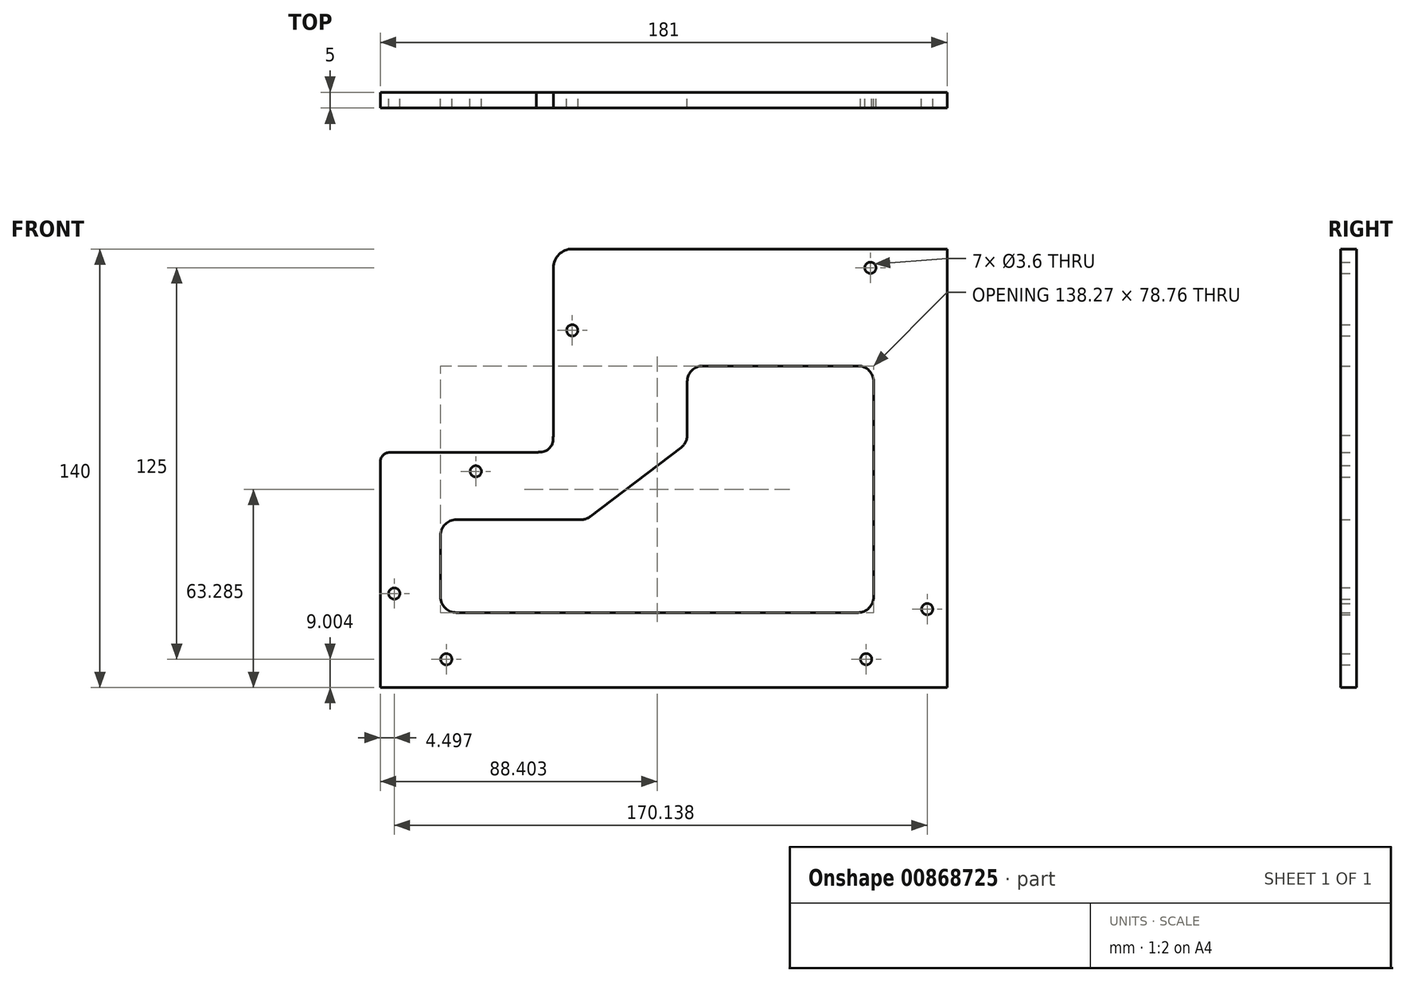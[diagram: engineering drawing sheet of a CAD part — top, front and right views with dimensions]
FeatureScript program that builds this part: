
annotation { "Feature Type Name" : "Feature", "Feature Type Description" : "" }
export const myFeature = defineFeature(function(context is Context, id is Id, definition is map)
    precondition{}
    {
        {
            var Q0;
            Q0=qCreatedBy(makeId("Front.planeOp"),FACE);
            var sketch = newSketch(context, id + "F0", { "sketchPlane" : qUnion([Q0])});
            skLineSegment(sketch, "E0", {"start": v(109.77, 85.1) * mm, "end": v(-9.9, 85.1) * mm});
            skLineSegment(sketch, "E1", {"start": v(-15.9, 79.1) * mm, "end": v(-15.9, 25.54) * mm});
            skLineSegment(sketch, "E2", {"start": v(-21.42, 20.1) * mm, "end": v(-68.23, 20.1) * mm});
            skLineSegment(sketch, "E3", {"start": v(-71.23, 17.1) * mm, "end": v(-71.23, -54.17) * mm});
            skLineSegment(sketch, "E4", {"start": v(-71.23, -54.9) * mm, "end": v(109.77, -54.9) * mm});
            skLineSegment(sketch, "E5", {"start": v(109.77, -54.17) * mm, "end": v(109.77, 85.1) * mm});
            skFitSpline(sketch, "E6", {"points": [v(-15.9, 25.54) * mm, v(-16.06, 24.58) * mm, v(-16.36, 22.68) * mm, v(-18.57, 20.52) * mm, v(-20.47, 20.24) * mm, v(-21.44, 20.1) * mm]});
            skLineSegment(sketch, "E7", {"start": v(-71.23, -54.17) * mm, "end": v(-71.23, -54.9) * mm});
            skLineSegment(sketch, "E8", {"start": v(109.77, -54.17) * mm, "end": v(109.77, -54.9) * mm});
            skCircle(sketch, "E9", {"center": v(85.27, 79.1) * mm, "radius": 1.8 * mm});
            skCircle(sketch, "E10", {"center": v(103.4, -29.9) * mm, "radius": 1.8 * mm});
            skCircle(sketch, "E11", {"center": v(83.94, -45.9) * mm, "radius": 1.8 * mm});
            skCircle(sketch, "E12", {"center": v(-50.14, -45.9) * mm, "radius": 1.8 * mm});
            skCircle(sketch, "E13", {"center": v(-66.73, -24.9) * mm, "radius": 1.8 * mm});
            skCircle(sketch, "E14", {"center": v(-40.73, 14.1) * mm, "radius": 1.8 * mm});
            skCircle(sketch, "E15", {"center": v(-9.9, 59.1) * mm, "radius": 1.8 * mm});
            skLineSegment(sketch, "E16.bottom", {"start": v(-46.96, -1.35) * mm, "end": v(-7.17, -1.35) * mm});
            skLineSegment(sketch, "E16.top", {"start": v(-46.96, -31) * mm, "end": v(81.3, -31) * mm});
            skLineSegment(sketch, "E16.left", {"start": v(-51.96, -6.35) * mm, "end": v(-51.96, -26) * mm});
            skLineSegment(sketch, "E16.right", {"start": v(86.3, -1.35) * mm, "end": v(86.3, -26) * mm});
            skLineSegment(sketch, "E17.top", {"start": v(81.3, 47.76) * mm, "end": v(31.8, 47.76) * mm});
            skLineSegment(sketch, "E17.left", {"start": v(86.3, -1.35) * mm, "end": v(86.3, 42.76) * mm});
            skLineSegment(sketch, "E17.right", {"start": v(26.8, 25.68) * mm, "end": v(26.8, 42.76) * mm});
            skPoint(sketch, "E18.visualSharp", {"position": v(26.8, 47.76) * mm});
            skArc(sketch, "E18.filletArc", {"start": v(31.8, 47.76) * mm, "mid": v(28.26, 46.3) * mm, "end": v(26.8, 42.76) * mm});
            skPoint(sketch, "E19.visualSharp", {"position": v(86.3, 47.76) * mm});
            skArc(sketch, "E19.filletArc", {"start": v(86.3, 42.76) * mm, "mid": v(84.84, 46.3) * mm, "end": v(81.3, 47.76) * mm});
            skPoint(sketch, "E20.visualSharp", {"position": v(86.3, -31) * mm});
            skArc(sketch, "E20.filletArc", {"start": v(81.3, -31) * mm, "mid": v(84.84, -29.54) * mm, "end": v(86.3, -26) * mm});
            skPoint(sketch, "E21.visualSharp", {"position": v(-51.96, -31) * mm});
            skArc(sketch, "E21.filletArc", {"start": v(-51.96, -26) * mm, "mid": v(-50.5, -29.54) * mm, "end": v(-46.96, -31) * mm});
            skPoint(sketch, "E22.visualSharp", {"position": v(-51.96, -1.35) * mm});
            skArc(sketch, "E22.filletArc", {"start": v(-46.96, -1.35) * mm, "mid": v(-50.5, -2.82) * mm, "end": v(-51.96, -6.35) * mm});
            skPoint(sketch, "E23.visualSharp", {"position": v(26.8, -1.35) * mm});
            skPoint(sketch, "E24.visualSharp", {"position": v(-15.9, 85.1) * mm});
            skArc(sketch, "E24.filletArc", {"start": v(-9.9, 85.1) * mm, "mid": v(-14.15, 83.34) * mm, "end": v(-15.9, 79.1) * mm});
            skPoint(sketch, "E25.visualSharp", {"position": v(-71.23, 20.1) * mm});
            skArc(sketch, "E25.filletArc", {"start": v(-68.23, 20.1) * mm, "mid": v(-70.35, 19.22) * mm, "end": v(-71.23, 17.1) * mm});
            skLineSegment(sketch, "E26", {"start": v(24.83, 21.7) * mm, "end": v(-4.14, -0.33) * mm});
            skPoint(sketch, "E23.filletArc.end.orphan", {"position": v(26.8, 3.65) * mm});
            skPoint(sketch, "E27.visualSharp", {"position": v(-5.49, -1.35) * mm});
            skArc(sketch, "E27.filletArc", {"start": v(-7.17, -1.35) * mm, "mid": v(-5.57, -1.1) * mm, "end": v(-4.14, -0.33) * mm});
            skPoint(sketch, "E28.visualSharp", {"position": v(26.8, 23.2) * mm});
            skArc(sketch, "E28.filletArc", {"start": v(24.83, 21.7) * mm, "mid": v(26.28, 23.46) * mm, "end": v(26.8, 25.68) * mm});
            skSolve(sketch);
        }
        {
            var Q0;
            Q0=makeQuery(id+"F0.imprint","IMPRINT",FACE,{"disambiguationData":[TD([[makeQuery(id+"F0.imprint","IMPRINT",EDGE,{"derivedFrom":sQuery(id+"F0.wireOp",EDGE,"E0")}),1.0]])]});
            extrude(context, id + "F1", {"entities" : qUnion([Q0]), "depth" : 5 * mm, "offsetDistance" : 25 * mm});
        }
    });
